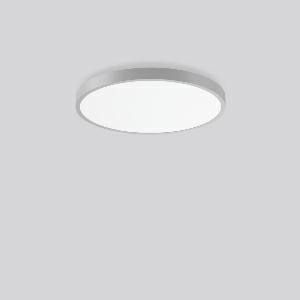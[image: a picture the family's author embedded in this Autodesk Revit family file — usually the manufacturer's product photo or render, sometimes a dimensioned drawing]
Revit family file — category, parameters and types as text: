
# Revit family: triona_round_a_312387_004_2_76_1634
name_source: partatom
category: Lighting Fixtures
units: mm (PartAtom-declared; Revit-internal decimal feet)

## family parameters
Cut with Voids When Loaded = No
Host = Face
Light Source = No
Part Type = Normal
Room Calculation Point = No
Round Connector Dimension = Use Diameter
Shared = No

## types (1)
- TuneableWhite 846 (1 x LED Modul 846, 4800 lm, 4600)
    Apparent Load = 49 VA
    CIE Flux Codes = 50 80 96 100 100
    Color Rendering = 80
    Color Temperature = 4600
    Default Elevation = 1800 mm
    Description = Series: TRIONA round
Decorative round LED surface-mounted luminaire. Flat, seamless frame: aluminium extrusion profile, powder coated. Cover made of sheet steel, powder-coated. Light emission through a diffuser: plastic, opal. Lightguide and diffuser made of non-yellowing plastic (PMMA). Lateral light emission (RZB SIDELITE technology) for above-average homogeneous light distribution. Tunable white versions, dynamically adjustable from 2700 K to 6500 K. Suitable for Ceiling mounting, Wall (surface). Tool-free mounting via bayonet connection. Electronic ballast included. Very easy installation thanks to Plug+Play connection. Ideal for use as part of the Human Centric Lighting concept in connection with RZB light management systems. 
Colour: silver, matt (approx. RAL 9006)
Diameter: 845 mm
Height: 88 mm
Lamp: LED
Socket: without socket
Colour temperature: 2700K - 6500K
Colour rendering index (CRI): 80
System power: 49 W
Rated luminous flux: 4800 lm
Luminous efficiency: 98 lm/W
System power 2: 51 W
Rated luminous flux 2: 4550 lm
Luminous efficiency 2: 89 lm/W
System power 3: 51 W
Rated luminous flux 3: 4650 lm
Luminous efficiency 3: 91 lm/W
Control gear: Converter, dimmable, DALI
Protection class: I
Type of protection: IP 20
    Height = 88 mm
    Lamp = 1 x LED Modul 846
    Lamp Light Flux = 4800 lm
    Lamp count = 1
    Length = 845 mm
    Lifetime = 50000 h
    Luminous efficacy = 98 lm/W
    Manufacturer = RZB
    ModVariant = No
    Model = 312387.004.2.76
    Mounting Place = Ceiling
    Mounting Type = Surface mounted
    Number of Poles = 1
    OnlyDefault = Yes
    Power Factor = 1
    Product Name = TRIONA round A
    Product group = Surface mounted modular luminaires
    ProductGroupID = 306
    Protection Class = Protection class I
    Protection Degree = IP 20
    RLX_Detail_Level = 1
    RLX_Emergency_Light_Flux = 0 lm
    RLX_Emergency_Type = 0
    RLX_Emergency_Type_DB = No
    RlxData = <blob elided: 32365 chars, md5=af15528e>
    Socket = socket
    Standby Power = 0 W
    System Light Flux = 4800 lm
    System Power = 49 W
    Type Comments = TuneableWhite 846
    Type Image = 312384.004.jpg
    URL = http://relux.com
    VarID = tuneablewhite_846
    Voltage = 230 V
    Voltage Range = 220-240 V
    Weight = 0.00 kg
    Width = 0 mm  [stored 0 ft]

note: [stored X ft] marks values corroborated as IEEE doubles in the binary element streams (Revit-internal decimal feet)

## geometry (parser evidence)
native form markers: Blend x4, Sweep x11
no freeform markers — native parametric forms only
